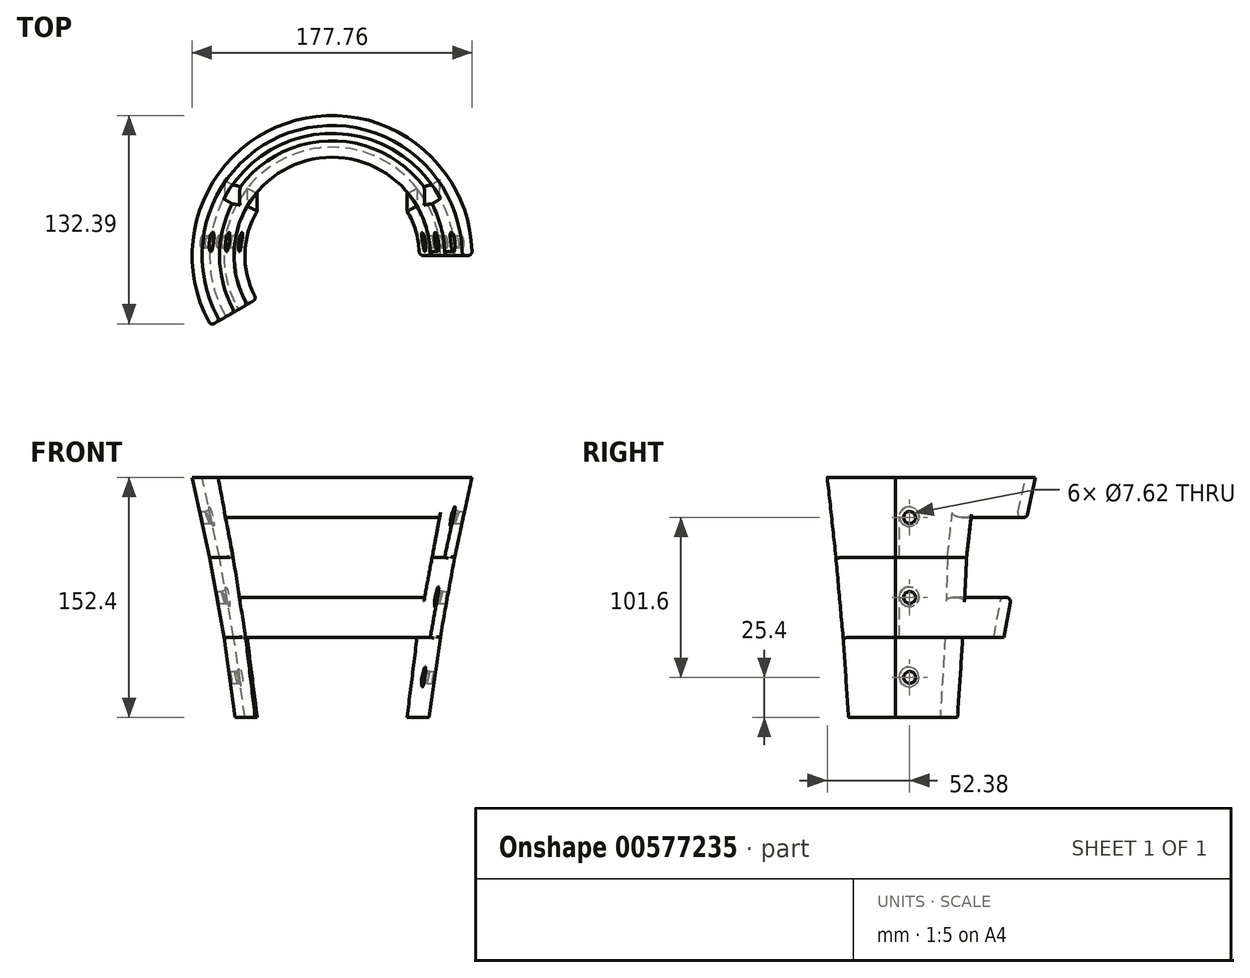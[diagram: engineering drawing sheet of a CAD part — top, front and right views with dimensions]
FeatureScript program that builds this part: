
annotation { "Feature Type Name" : "Feature", "Feature Type Description" : "" }
export const myFeature = defineFeature(function(context is Context, id is Id, definition is map)
    precondition{}
    {
        {
            var Q0;
            Q0=qCreatedBy(makeId("Front.planeOp"),FACE);
            var sketch = newSketch(context, id + "F0", { "sketchPlane" : qUnion([Q0])});
            skLineSegment(sketch, "E0", {"start": v(0, 0) * mm, "end": v(0, 50.8) * mm});
            skLineSegment(sketch, "E1", {"start": v(0, 50.8) * mm, "end": v(68.76, 50.8) * mm, "construction": true});
            skLineSegment(sketch, "E2", {"start": v(0, 0) * mm, "end": v(61.72, 0) * mm});
            skLineSegment(sketch, "E3", {"start": v(61.72, 0) * mm, "end": v(68.76, 50.8) * mm});
            skLineSegment(sketch, "E4", {"start": v(0, 50.8) * mm, "end": v(0, 101.6) * mm});
            skLineSegment(sketch, "E5", {"start": v(0, 101.6) * mm, "end": v(77.84, 101.6) * mm, "construction": true});
            skLineSegment(sketch, "E6", {"start": v(77.84, 101.6) * mm, "end": v(68.76, 50.8) * mm});
            skLineSegment(sketch, "E7", {"start": v(0, 101.6) * mm, "end": v(0, 152.4) * mm});
            skLineSegment(sketch, "E8", {"start": v(0, 152.4) * mm, "end": v(88.9, 152.4) * mm});
            skLineSegment(sketch, "E9", {"start": v(88.9, 152.4) * mm, "end": v(77.84, 101.6) * mm});
            skSolve(sketch);
        }
        {
            var Q0;
            Q0=qSketchRegion(id+"F0",true);
            var Q1;
            Q1=sQuery(id+"F0.wireOp",EDGE,"E7");
            revolve(context, id + "F1", {"entities" : qUnion([Q0]), "axis" : qUnion([Q1]), "revolveType" : RevolveType.ONE_DIRECTION, "angle" : 210 * degree});
        }
        {
            var Q0;
            Q0=qCreatedBy(makeId("Front.planeOp"),FACE);
            var sketch = newSketch(context, id + "F2", { "sketchPlane" : qUnion([Q0])});
            skLineSegment(sketch, "E10", {"start": v(0, 50.8) * mm, "end": v(62.4, 50.8) * mm, "construction": true});
            skLineSegment(sketch, "E11", {"start": v(0, 50.8) * mm, "end": v(0, 101.6) * mm});
            skLineSegment(sketch, "E12", {"start": v(0, 101.6) * mm, "end": v(71.49, 101.6) * mm, "construction": true});
            skLineSegment(sketch, "E13", {"start": v(71.49, 101.6) * mm, "end": v(62.4, 50.8) * mm});
            skLineSegment(sketch, "E14", {"start": v(0, 101.6) * mm, "end": v(0, 152.4) * mm});
            skLineSegment(sketch, "E15", {"start": v(0, 152.4) * mm, "end": v(82.55, 152.4) * mm});
            skLineSegment(sketch, "E16", {"start": v(82.55, 152.4) * mm, "end": v(71.49, 101.6) * mm});
            skPoint(sketch, "E17.start.orphan", {"position": v(1.44, 0) * mm});
            skLineSegment(sketch, "E18", {"start": v(0, 50.8) * mm, "end": v(0, 0) * mm});
            skLineSegment(sketch, "E19", {"start": v(0, 0) * mm, "end": v(55.37, 0) * mm});
            skLineSegment(sketch, "E20", {"start": v(55.37, 0) * mm, "end": v(62.4, 50.8) * mm});
            skSolve(sketch);
        }
        {
            var Q0;
            Q0=qCreatedBy(makeId("Right.planeOp"),FACE);
            var sketch = newSketch(context, id + "F3", { "sketchPlane" : qUnion([Q0])});
            skLineSegment(sketch, "E21", {"start": v(0, 152.4) * mm, "end": v(88.9, 152.4) * mm, "construction": true});
            skLineSegment(sketch, "E22", {"start": v(0, 0) * mm, "end": v(75.6, 0) * mm, "construction": true});
            skLineSegment(sketch, "E23", {"start": v(0, 0) * mm, "end": v(0, 50.8) * mm, "construction": true});
            skLineSegment(sketch, "E24", {"start": v(0, 50.8) * mm, "end": v(0, 101.6) * mm, "construction": true});
            skLineSegment(sketch, "E25", {"start": v(0, 101.6) * mm, "end": v(0, 152.4) * mm, "construction": true});
            skLineSegment(sketch, "E26", {"start": v(0, 50.8) * mm, "end": v(125.48, 50.8) * mm, "construction": true});
            skLineSegment(sketch, "E27", {"start": v(0, 101.6) * mm, "end": v(125.48, 101.6) * mm, "construction": true});
            skPoint(sketch, "E28", {"position": v(8.89, 25.4) * mm});
            skPoint(sketch, "E28.positionSnap0", {"position": v(0, 25.4) * mm});
            skPoint(sketch, "E29", {"position": v(9.48, 79.82) * mm});
            skPoint(sketch, "E30", {"position": v(0, 76.2) * mm});
            skCircle(sketch, "E31", {"center": v(8.89, 25.4) * mm, "radius": 3.81 * mm});
            skLineSegment(sketch, "E32", {"start": v(0, 76.2) * mm, "end": v(116.66, 76.2) * mm, "construction": true});
            skPoint(sketch, "E33", {"position": v(0, 127) * mm});
            skLineSegment(sketch, "E34", {"start": v(0, 127) * mm, "end": v(163.8, 127) * mm, "construction": true});
            skLineSegment(sketch, "E35", {"start": v(8.89, 25.4) * mm, "end": v(8.89, 161.7) * mm, "construction": true});
            skPoint(sketch, "E36", {"position": v(8.89, 127) * mm});
            skPoint(sketch, "E37", {"position": v(8.89, 76.2) * mm});
            skCircle(sketch, "E38", {"center": v(8.89, 76.2) * mm, "radius": 3.81 * mm});
            skCircle(sketch, "E39", {"center": v(8.89, 127) * mm, "radius": 3.81 * mm});
            skSolve(sketch);
        }
        {
            var Q0;
            Q0=qSketchRegion(id+"F3",true);
            extrude(context, id + "F4", {"entities" : qUnion([Q0]), "operationType" : NewBodyOperationType.REMOVE, "endBound" : BoundingType.SYMMETRIC, "oppositeDirection" : true, "depth" : 1270 * mm, "offsetDistance" : 25.4 * mm});
        }
        {
            var Q0;
            Q0=qSketchRegion(id+"F2",true);
            var Q1;
            Q1=sQuery(id+"F2.wireOp",EDGE,"E14");
            revolve(context, id + "F5", {"operationType" : NewBodyOperationType.REMOVE, "entities" : qUnion([Q0]), "axis" : qUnion([Q1]), "revolveType" : RevolveType.FULL, "oppositeDirection" : true});
        }
        {
            var Q0;
            Q0=qCreatedBy(makeId("Front.planeOp"),FACE);
            var sketch = newSketch(context, id + "F6", { "sketchPlane" : qUnion([Q0])});
            skLineSegment(sketch, "E40.bottom", {"start": v(41.28, 50.8) * mm, "end": v(-41.28, 50.8) * mm});
            skPoint(sketch, "E40.middle", {"position": v(0, 0) * mm});
            skLineSegment(sketch, "E41", {"start": v(41.28, 50.8) * mm, "end": v(53.98, 50.8) * mm});
            skLineSegment(sketch, "E42", {"start": v(53.98, 50.8) * mm, "end": v(47.62, 0) * mm});
            skLineSegment(sketch, "E43", {"start": v(47.63, 0) * mm, "end": v(41.28, 0) * mm});
            skLineSegment(sketch, "E44", {"start": v(41.28, 0) * mm, "end": v(-41.28, 0) * mm});
            skLineSegment(sketch, "E45", {"start": v(-41.28, 0) * mm, "end": v(-47.63, 0) * mm});
            skLineSegment(sketch, "E46", {"start": v(-41.28, 50.8) * mm, "end": v(-53.98, 50.8) * mm});
            skLineSegment(sketch, "E47", {"start": v(-53.98, 50.8) * mm, "end": v(-47.63, 0) * mm});
            skLineSegment(sketch, "E48", {"start": v(0, 0) * mm, "end": v(0, 101.6) * mm, "construction": true});
            skLineSegment(sketch, "E49.bottom", {"start": v(58.74, 76.2) * mm, "end": v(-58.74, 76.2) * mm});
            skLineSegment(sketch, "E49.top", {"start": v(58.74, 127) * mm, "end": v(-58.74, 127) * mm});
            skLineSegment(sketch, "E49.left", {"start": v(58.74, 76.2) * mm, "end": v(58.74, 127) * mm, "construction": true});
            skLineSegment(sketch, "E49.right", {"start": v(-58.74, 76.2) * mm, "end": v(-58.74, 127) * mm, "construction": true});
            skPoint(sketch, "E49.middle", {"position": v(0, 101.6) * mm});
            skLineSegment(sketch, "E50", {"start": v(58.74, 127) * mm, "end": v(68.26, 127) * mm});
            skLineSegment(sketch, "E51", {"start": v(-58.74, 127) * mm, "end": v(-68.26, 127) * mm});
            skLineSegment(sketch, "E52", {"start": v(-68.26, 127) * mm, "end": v(-58.74, 76.2) * mm});
            skLineSegment(sketch, "E53", {"start": v(68.26, 127) * mm, "end": v(58.74, 76.2) * mm});
            skSolve(sketch);
        }
        {
            var Q0;
            Q0 = qSketchRegion(id + "F6", true);
            extrude(context, id + "F7", {"entities" : qUnion([Q0]), "operationType" : NewBodyOperationType.REMOVE, "oppositeDirection" : true, "depth" : 101.6 * mm, "offsetDistance" : 25.4 * mm});
        }
        {
            var Q0;
            Q0=makeQuery(id+"F5.boolean.opBoolean","INTERSECT",EDGE,{"derivedFrom":[makeQuery(id+"F1.opRevolve","CAP_FACE",FACE,{"disambiguationData":[OSD([sQuery(id+"F0.wireOp",EDGE,"E0"),sQuery(id+"F0.wireOp",EDGE,"E2"),sQuery(id+"F0.wireOp",EDGE,"E3"),sQuery(id+"F0.wireOp",EDGE,"E4"),sQuery(id+"F0.wireOp",EDGE,"E6"),sQuery(id+"F0.wireOp",EDGE,"E7"),sQuery(id+"F0.wireOp",EDGE,"E8"),sQuery(id+"F0.wireOp",EDGE,"E9")])],"isStart":false}),makeQuery(id+"F5.opRevolve","SWEPT_FACE",FACE,{"disambiguationData":[OSD([sQuery(id+"F2.wireOp",EDGE,"E16")])]})]});
            var Q1;
            Q1=makeQuery(id+"F5.boolean.opBoolean","INTERSECT",EDGE,{"derivedFrom":[makeQuery(id+"F1.opRevolve","CAP_FACE",FACE,{"disambiguationData":[OSD([sQuery(id+"F0.wireOp",EDGE,"E0"),sQuery(id+"F0.wireOp",EDGE,"E2"),sQuery(id+"F0.wireOp",EDGE,"E3"),sQuery(id+"F0.wireOp",EDGE,"E4"),sQuery(id+"F0.wireOp",EDGE,"E6"),sQuery(id+"F0.wireOp",EDGE,"E7"),sQuery(id+"F0.wireOp",EDGE,"E8"),sQuery(id+"F0.wireOp",EDGE,"E9")])],"isStart":false}),makeQuery(id+"F5.opRevolve","SWEPT_FACE",FACE,{"disambiguationData":[OSD([sQuery(id+"F2.wireOp",EDGE,"E13")])]})]});
            var Q2;
            Q2=makeQuery(id+"F5.boolean.opBoolean","INTERSECT",EDGE,{"derivedFrom":[makeQuery(id+"F1.opRevolve","CAP_FACE",FACE,{"disambiguationData":[OSD([sQuery(id+"F0.wireOp",EDGE,"E0"),sQuery(id+"F0.wireOp",EDGE,"E2"),sQuery(id+"F0.wireOp",EDGE,"E3"),sQuery(id+"F0.wireOp",EDGE,"E4"),sQuery(id+"F0.wireOp",EDGE,"E6"),sQuery(id+"F0.wireOp",EDGE,"E7"),sQuery(id+"F0.wireOp",EDGE,"E8"),sQuery(id+"F0.wireOp",EDGE,"E9")])],"isStart":false}),makeQuery(id+"F5.opRevolve","SWEPT_FACE",FACE,{"disambiguationData":[OSD([sQuery(id+"F2.wireOp",EDGE,"E20")])]})]});
            var Q3;
            Q3=makeQuery(id+"F1.opRevolve","CAP_EDGE",EDGE,{"disambiguationData":[OSD([sQuery(id+"F0.wireOp",EDGE,"E9")])],"isStart":false});
            var Q4;
            Q4=makeQuery(id+"F1.opRevolve","CAP_EDGE",EDGE,{"disambiguationData":[OSD([sQuery(id+"F0.wireOp",EDGE,"E6")])],"isStart":false});
            var Q5;
            Q5=makeQuery(id+"F1.opRevolve","CAP_EDGE",EDGE,{"disambiguationData":[OSD([sQuery(id+"F0.wireOp",EDGE,"E3")])],"isStart":false});
            var Q6;
            Q6=makeQuery(id+"F5.boolean.opBoolean","INTERSECT",EDGE,{"derivedFrom":[makeQuery(id+"F1.opRevolve","CAP_FACE",FACE,{"disambiguationData":[OSD([sQuery(id+"F0.wireOp",EDGE,"E0"),sQuery(id+"F0.wireOp",EDGE,"E2"),sQuery(id+"F0.wireOp",EDGE,"E3"),sQuery(id+"F0.wireOp",EDGE,"E4"),sQuery(id+"F0.wireOp",EDGE,"E6"),sQuery(id+"F0.wireOp",EDGE,"E7"),sQuery(id+"F0.wireOp",EDGE,"E8"),sQuery(id+"F0.wireOp",EDGE,"E9")])],"isStart":true}),makeQuery(id+"F5.opRevolve","SWEPT_FACE",FACE,{"disambiguationData":[OSD([sQuery(id+"F2.wireOp",EDGE,"E16")])]})]});
            var Q7;
            Q7=makeQuery(id+"F5.boolean.opBoolean","INTERSECT",EDGE,{"disambiguationData":[OD(0.0)],"derivedFrom":[makeQuery(id+"F4.boolean.opBoolean","COPY",FACE,{"derivedFrom":makeQuery(id+"F4.opExtrude","SWEPT_FACE",FACE,{"disambiguationData":[OSD([sQuery(id+"F3.wireOp",EDGE,"E39")])]})}),makeQuery(id+"F5.opRevolve","SWEPT_FACE",FACE,{"disambiguationData":[OSD([sQuery(id+"F2.wireOp",EDGE,"E16")])]})]});
            var Q8;
            Q8=makeQuery(id+"F5.boolean.opBoolean","INTERSECT",EDGE,{"disambiguationData":[OD(1.0)],"derivedFrom":[makeQuery(id+"F4.boolean.opBoolean","COPY",FACE,{"derivedFrom":makeQuery(id+"F4.opExtrude","SWEPT_FACE",FACE,{"disambiguationData":[OSD([sQuery(id+"F3.wireOp",EDGE,"E39")])]})}),makeQuery(id+"F5.opRevolve","SWEPT_FACE",FACE,{"disambiguationData":[OSD([sQuery(id+"F2.wireOp",EDGE,"E16")])]})]});
            var Q9;
            Q9=makeQuery(id+"F5.boolean.opBoolean","INTERSECT",EDGE,{"derivedFrom":[makeQuery(id+"F1.opRevolve","CAP_FACE",FACE,{"disambiguationData":[OSD([sQuery(id+"F0.wireOp",EDGE,"E0"),sQuery(id+"F0.wireOp",EDGE,"E2"),sQuery(id+"F0.wireOp",EDGE,"E3"),sQuery(id+"F0.wireOp",EDGE,"E4"),sQuery(id+"F0.wireOp",EDGE,"E6"),sQuery(id+"F0.wireOp",EDGE,"E7"),sQuery(id+"F0.wireOp",EDGE,"E8"),sQuery(id+"F0.wireOp",EDGE,"E9")])],"isStart":true}),makeQuery(id+"F5.opRevolve","SWEPT_FACE",FACE,{"disambiguationData":[OSD([sQuery(id+"F2.wireOp",EDGE,"E13")])]})]});
            var Q10;
            Q10=makeQuery(id+"F5.boolean.opBoolean","INTERSECT",EDGE,{"disambiguationData":[OD(0.0)],"derivedFrom":[makeQuery(id+"F4.boolean.opBoolean","COPY",FACE,{"derivedFrom":makeQuery(id+"F4.opExtrude","SWEPT_FACE",FACE,{"disambiguationData":[OSD([sQuery(id+"F3.wireOp",EDGE,"E38")])]})}),makeQuery(id+"F5.opRevolve","SWEPT_FACE",FACE,{"disambiguationData":[OSD([sQuery(id+"F2.wireOp",EDGE,"E13")])]})]});
            var Q11;
            Q11=makeQuery(id+"F5.boolean.opBoolean","INTERSECT",EDGE,{"disambiguationData":[OD(1.0)],"derivedFrom":[makeQuery(id+"F4.boolean.opBoolean","COPY",FACE,{"derivedFrom":makeQuery(id+"F4.opExtrude","SWEPT_FACE",FACE,{"disambiguationData":[OSD([sQuery(id+"F3.wireOp",EDGE,"E38")])]})}),makeQuery(id+"F5.opRevolve","SWEPT_FACE",FACE,{"disambiguationData":[OSD([sQuery(id+"F2.wireOp",EDGE,"E13")])]})]});
            var Q12;
            Q12=makeQuery(id+"F5.boolean.opBoolean","INTERSECT",EDGE,{"derivedFrom":[makeQuery(id+"F1.opRevolve","CAP_FACE",FACE,{"disambiguationData":[OSD([sQuery(id+"F0.wireOp",EDGE,"E0"),sQuery(id+"F0.wireOp",EDGE,"E2"),sQuery(id+"F0.wireOp",EDGE,"E3"),sQuery(id+"F0.wireOp",EDGE,"E4"),sQuery(id+"F0.wireOp",EDGE,"E6"),sQuery(id+"F0.wireOp",EDGE,"E7"),sQuery(id+"F0.wireOp",EDGE,"E8"),sQuery(id+"F0.wireOp",EDGE,"E9")])],"isStart":true}),makeQuery(id+"F5.opRevolve","SWEPT_FACE",FACE,{"disambiguationData":[OSD([sQuery(id+"F2.wireOp",EDGE,"E20")])]})]});
            var Q13;
            Q13=makeQuery(id+"F5.boolean.opBoolean","INTERSECT",EDGE,{"disambiguationData":[OD(0.0)],"derivedFrom":[makeQuery(id+"F4.boolean.opBoolean","COPY",FACE,{"derivedFrom":makeQuery(id+"F4.opExtrude","SWEPT_FACE",FACE,{"disambiguationData":[OSD([sQuery(id+"F3.wireOp",EDGE,"E31")])]})}),makeQuery(id+"F5.opRevolve","SWEPT_FACE",FACE,{"disambiguationData":[OSD([sQuery(id+"F2.wireOp",EDGE,"E20")])]})]});
            var Q14;
            Q14=makeQuery(id+"F5.boolean.opBoolean","INTERSECT",EDGE,{"disambiguationData":[OD(1.0)],"derivedFrom":[makeQuery(id+"F4.boolean.opBoolean","COPY",FACE,{"derivedFrom":makeQuery(id+"F4.opExtrude","SWEPT_FACE",FACE,{"disambiguationData":[OSD([sQuery(id+"F3.wireOp",EDGE,"E31")])]})}),makeQuery(id+"F5.opRevolve","SWEPT_FACE",FACE,{"disambiguationData":[OSD([sQuery(id+"F2.wireOp",EDGE,"E20")])]})]});
            var Q15;
            Q15=makeQuery(id+"F7.boolean.opBoolean","INTERSECT",EDGE,{"derivedFrom":[makeQuery(id+"F5.boolean.opBoolean","COPY",FACE,{"derivedFrom":makeQuery(id+"F5.opRevolve","SWEPT_FACE",FACE,{"disambiguationData":[OSD([sQuery(id+"F2.wireOp",EDGE,"E13")])]})}),makeQuery(id+"F7.opExtrude","SWEPT_FACE",FACE,{"disambiguationData":[OSD([sQuery(id+"F6.wireOp",EDGE,"E49.bottom")])]})]});
            var Q16;
            Q16=makeQuery(id+"F7.boolean.opBoolean","INTERSECT",EDGE,{"derivedFrom":[makeQuery(id+"F1.opRevolve","SWEPT_FACE",FACE,{"disambiguationData":[OSD([sQuery(id+"F0.wireOp",EDGE,"E6")])]}),makeQuery(id+"F7.opExtrude","SWEPT_FACE",FACE,{"disambiguationData":[OSD([sQuery(id+"F6.wireOp",EDGE,"E49.bottom")])]})]});
            var Q17;
            Q17=makeQuery(id+"F7.boolean.opBoolean","INTERSECT",EDGE,{"derivedFrom":[makeQuery(id+"F5.boolean.opBoolean","COPY",FACE,{"derivedFrom":makeQuery(id+"F5.opRevolve","SWEPT_FACE",FACE,{"disambiguationData":[OSD([sQuery(id+"F2.wireOp",EDGE,"E16")])]})}),makeQuery(id+"F7.opExtrude","SWEPT_FACE",FACE,{"disambiguationData":[OSD([sQuery(id+"F6.wireOp",EDGE,"E49.top"),sQuery(id+"F6.wireOp",EDGE,"E50"),sQuery(id+"F6.wireOp",EDGE,"E51")])]})]});
            var Q18;
            Q18=makeQuery(id+"F7.boolean.opBoolean","INTERSECT",EDGE,{"derivedFrom":[makeQuery(id+"F1.opRevolve","SWEPT_FACE",FACE,{"disambiguationData":[OSD([sQuery(id+"F0.wireOp",EDGE,"E9")])]}),makeQuery(id+"F7.opExtrude","SWEPT_FACE",FACE,{"disambiguationData":[OSD([sQuery(id+"F6.wireOp",EDGE,"E49.top"),sQuery(id+"F6.wireOp",EDGE,"E50"),sQuery(id+"F6.wireOp",EDGE,"E51")])]})]});
            var Q19;
            Q19=makeQuery(id+"F1.opRevolve","CAP_EDGE",EDGE,{"disambiguationData":[OSD([sQuery(id+"F0.wireOp",EDGE,"E9")])],"isStart":true});
            var Q20;
            Q20=makeQuery(id+"F1.opRevolve","CAP_EDGE",EDGE,{"disambiguationData":[OSD([sQuery(id+"F0.wireOp",EDGE,"E6")])],"isStart":true});
            fillet(context, id + "F8", {"entities" : qUnion([Q0, Q1, Q2, Q3, Q4, Q5, Q6, Q7, Q8, Q9, Q10, Q11, Q12, Q13, Q14, Q15, Q16, Q17, Q18, Q19, Q20]), "radius" : 2.54 * mm, "tangentPropagation" : true, "allowEdgeOverflow" : false});
        }
    });
